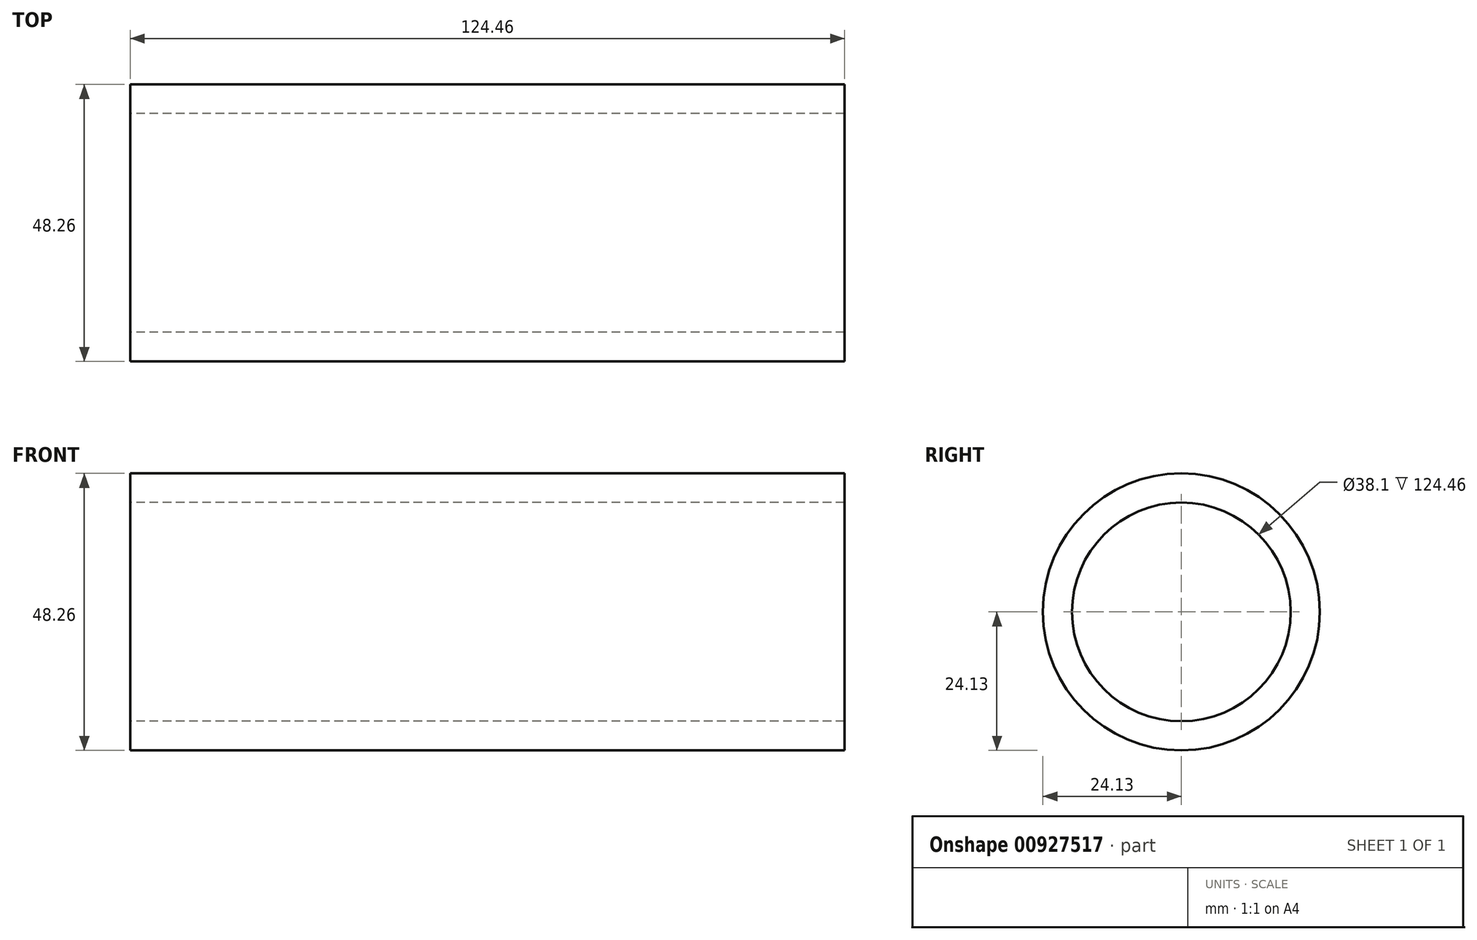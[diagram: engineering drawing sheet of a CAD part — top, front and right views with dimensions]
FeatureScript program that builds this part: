
annotation { "Feature Type Name" : "Feature", "Feature Type Description" : "" }
export const myFeature = defineFeature(function(context is Context, id is Id, definition is map)
    precondition{}
    {
        {
            var Q0;
            Q0=qCreatedBy(makeId("Right.planeOp"),FACE);
            var sketch = newSketch(context, id + "F0", { "sketchPlane" : qUnion([Q0])});
            skCircle(sketch, "E0", {"center": v(0, 0) * mm, "radius": 24.13 * mm});
            skCircle(sketch, "E1", {"center": v(0, 0) * mm, "radius": 19.05 * mm});
            skSolve(sketch);
        }
        {
            var Q0;
            Q0=makeQuery(id+"F0.imprint","IMPRINT",FACE,{"disambiguationData":[TD([[makeQuery(id+"F0.imprint","IMPRINT",EDGE,{"derivedFrom":sQuery(id+"F0.wireOp",EDGE,"E0")}),1.0]])]});
            extrude(context, id + "F1", {"entities" : qUnion([Q0]), "depth" : 124.46 * mm, "offsetDistance" : 25.4 * mm});
        }
    });
